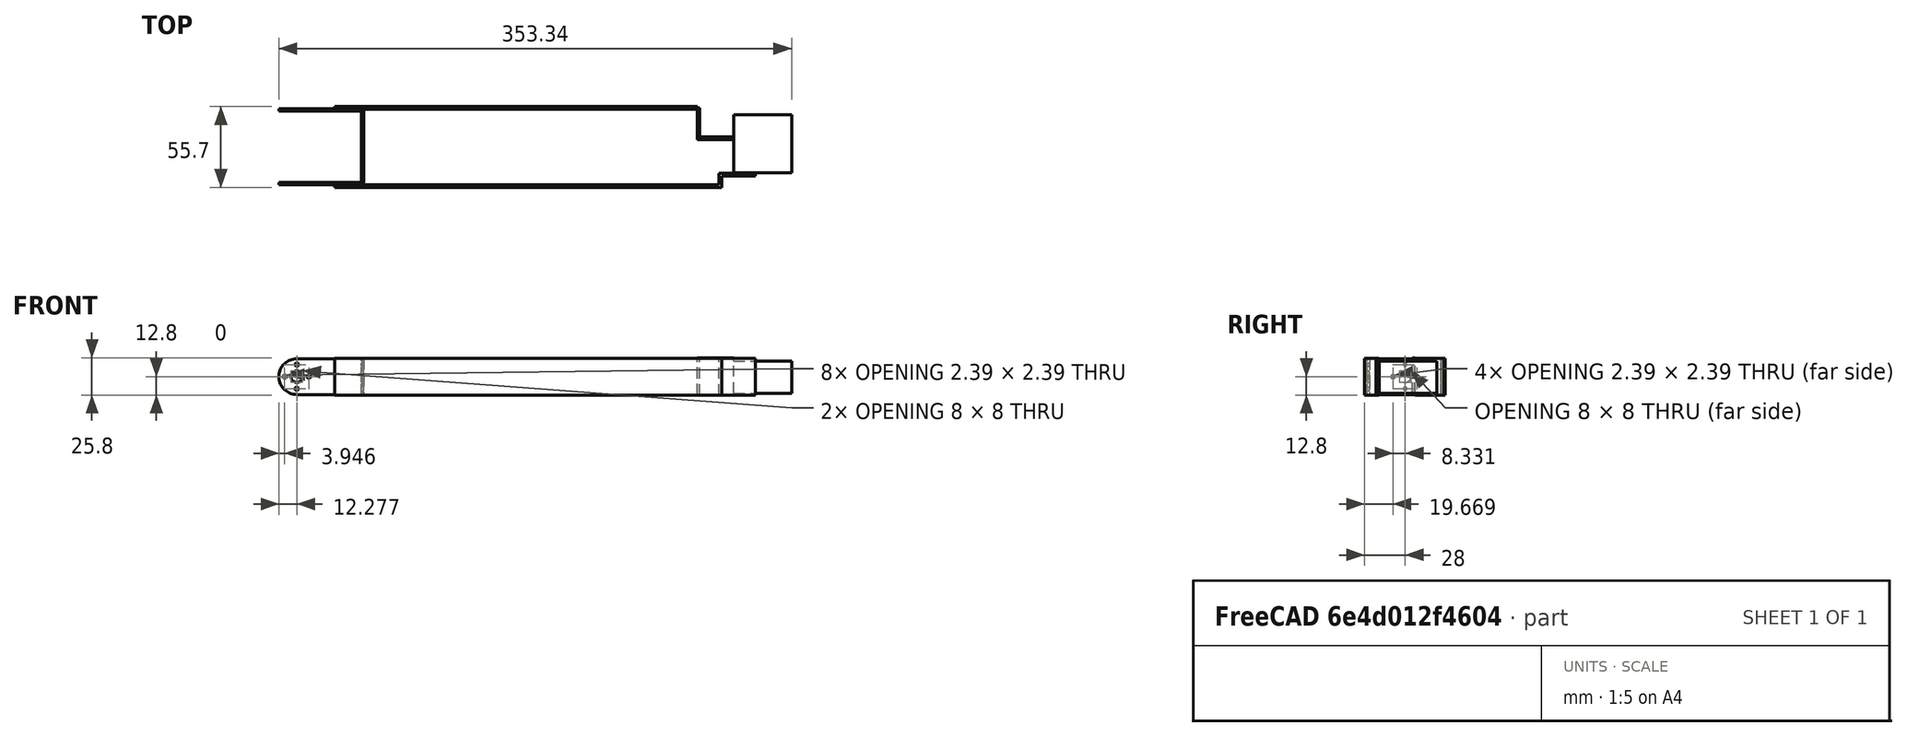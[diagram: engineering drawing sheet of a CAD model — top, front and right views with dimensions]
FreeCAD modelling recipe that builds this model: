
FCSTD DOCUMENT
Label: UpperArm
objects: Part::Box×7, Part::MultiFuse×3, Part::Feature×1
note: 11 computed .brp shape members not serialized (recipe doc carries the construction recipe); baked Part::Feature solids carry a one-line shape summary decoded from their .brp

FEATURE [Part::Feature] asb_10
  Placement = pos=(0,0,0) rot=(0,0,1;1.5708rad)
  shape: bbox 58.34 x 52.25 x 24.61 mm, 48 faces (baked)
FEATURE [Part::Box] Box
  Height = 25.4
  Length = 265
  Placement = pos=(-20,-28,-12.8) rot=(0,0,1;0rad)
  Width = 1.7
FEATURE [Part::Box] Box001
  Height = 25.4
  Length = 1.7
  Placement = pos=(245,-28,-12.8) rot=(0,0,1;0rad)
  Width = 8
FEATURE [Part::Box] Box002
  Height = 25.4
  Length = 25
  Placement = pos=(245,-20,-12.8) rot=(0,0,1;0rad)
  Width = 1.7
FEATURE [Part::MultiFuse] Fusion
  Shapes = -> [Box002,Box,Box001]
FEATURE [Part::Box] Box003
  Height = 25.4
  Length = 250
  Placement = pos=(-20,26,-12.8) rot=(0,0,1;0rad)
  Width = 1.7
FEATURE [Part::Box] Box004
  Height = 25.4
  Length = 1.7
  Placement = pos=(230,7,-12.8) rot=(0,0,1;0rad)
  Width = 20
FEATURE [Part::Box] Box005
  Height = 25.4
  Length = 25
  Placement = pos=(230,5,-12.4) rot=(0,0,1;0rad)
  Width = 1.7
FEATURE [Part::MultiFuse] Fusion001
  Shapes = -> [Box005,Box003,Box004]
FEATURE [Part::Box] Box006  label="Servo 2"
  Height = 22
  Length = 40
  Placement = pos=(255,-18,-11.4) rot=(0,0,1;0rad)
  Width = 40
FEATURE [Part::MultiFuse] Fusion002  label="Upper Arm"
  Shapes = -> [asb_10,Fusion,Fusion001,Box006]
